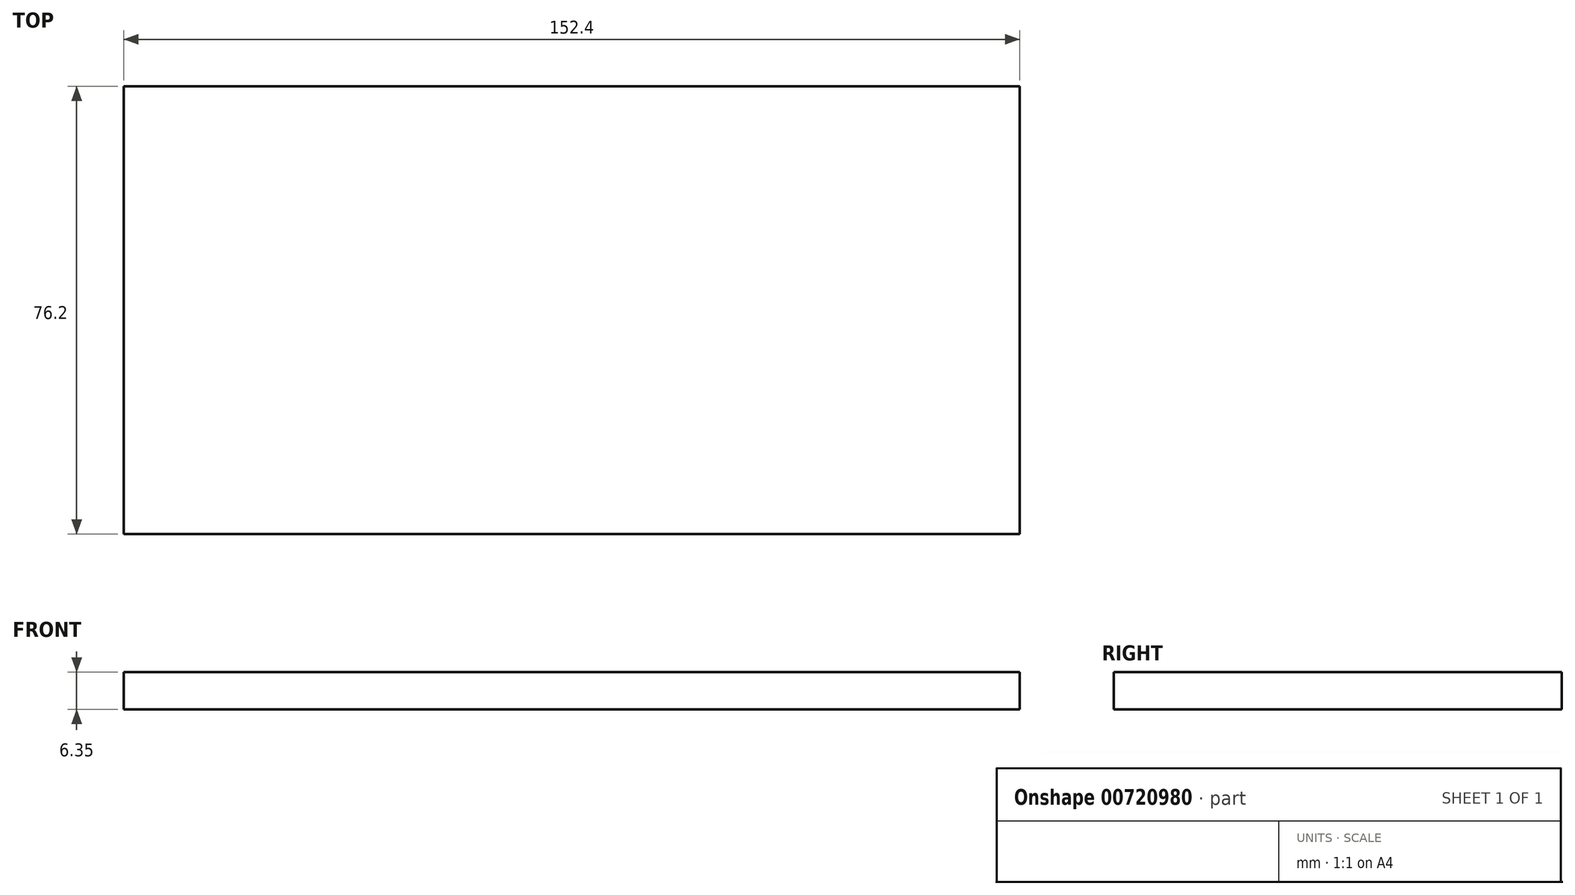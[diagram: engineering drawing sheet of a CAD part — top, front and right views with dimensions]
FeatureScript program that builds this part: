
annotation { "Feature Type Name" : "Feature", "Feature Type Description" : "" }
export const myFeature = defineFeature(function(context is Context, id is Id, definition is map)
    precondition{}
    {
        {
            var Q0;
            Q0=qCreatedBy(makeId("Top.planeOp"),FACE);
            var sketch = newSketch(context, id + "F0", { "sketchPlane" : qUnion([Q0])});
            skLineSegment(sketch, "E0.bottom", {"start": v(-76.08, 30.78) * mm, "end": v(76.32, 30.78) * mm});
            skLineSegment(sketch, "E0.top", {"start": v(-76.08, -45.42) * mm, "end": v(76.32, -45.42) * mm});
            skLineSegment(sketch, "E0.left", {"start": v(-76.08, 30.78) * mm, "end": v(-76.08, -45.42) * mm});
            skLineSegment(sketch, "E0.right", {"start": v(76.32, 30.78) * mm, "end": v(76.32, -45.42) * mm});
            skSolve(sketch);
        }
        {
            var Q0;
            Q0 = qSketchRegion(id + "F0", true);
            extrude(context, id + "F1", {"entities" : qUnion([Q0]), "oppositeDirection" : true, "depth" : 6.35 * mm, "offsetDistance" : 25.4 * mm});
        }
    });
